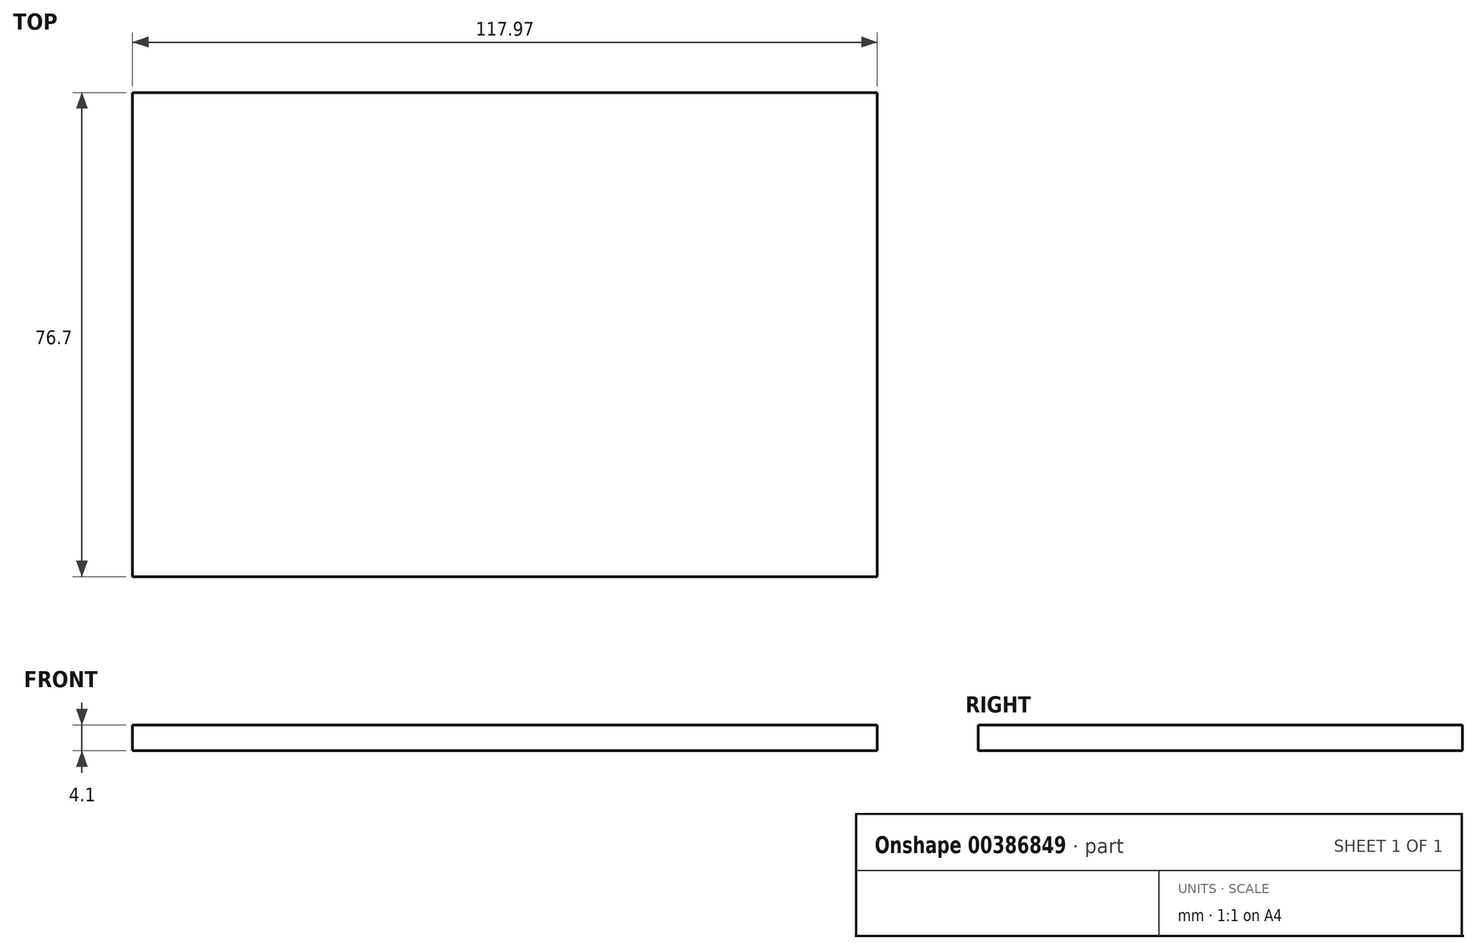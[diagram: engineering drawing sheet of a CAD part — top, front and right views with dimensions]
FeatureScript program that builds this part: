
annotation { "Feature Type Name" : "Feature", "Feature Type Description" : "" }
export const myFeature = defineFeature(function(context is Context, id is Id, definition is map)
    precondition{}
    {
        {
            var Q0;
            Q0=qCreatedBy(makeId("Front.planeOp"),FACE);
            var sketch = newSketch(context, id + "F0", { "sketchPlane" : qUnion([Q0])});
            skLineSegment(sketch, "E0.bottom", {"start": v(-55.1, 18.55) * mm, "end": v(62.87, 18.55) * mm});
            skLineSegment(sketch, "E0.top", {"start": v(-55.1, 14.45) * mm, "end": v(62.87, 14.45) * mm});
            skLineSegment(sketch, "E0.left", {"start": v(-55.1, 18.55) * mm, "end": v(-55.1, 14.45) * mm});
            skLineSegment(sketch, "E0.right", {"start": v(62.87, 18.55) * mm, "end": v(62.87, 14.45) * mm});
            skSolve(sketch);
        }
        {
            var Q0;
            Q0=makeQuery(id+"F0.imprint","IMPRINT",FACE,{"disambiguationData":[TD([[makeQuery(id+"F0.imprint","IMPRINT",EDGE,{"derivedFrom":sQuery(id+"F0.wireOp",EDGE,"E0.bottom")}),-1.0]])]});
            extrude(context, id + "F1", {"entities" : qUnion([Q0]), "endBound" : BoundingType.SYMMETRIC, "depth" : 76.7 * mm});
        }
        {
            var Q0;
            Q0=makeQuery(id+"F1.opExtrude","SWEPT_BODY",BODY,{"disambiguationData":[OSD([sQuery(id+"F0.wireOp",EDGE,"E0.bottom"),sQuery(id+"F0.wireOp",EDGE,"E0.top"),sQuery(id+"F0.wireOp",EDGE,"E0.left"),sQuery(id+"F0.wireOp",EDGE,"E0.right")])]});
            transform(context, id + "F2", {"entities" : qUnion([Q0]), "transformType" : TransformType.TRANSLATION_3D, "dx" : -3.8 * mm, "dy" : 0 * mm, "dz" : 0 * mm, "makeCopy" : false});
        }
    });
